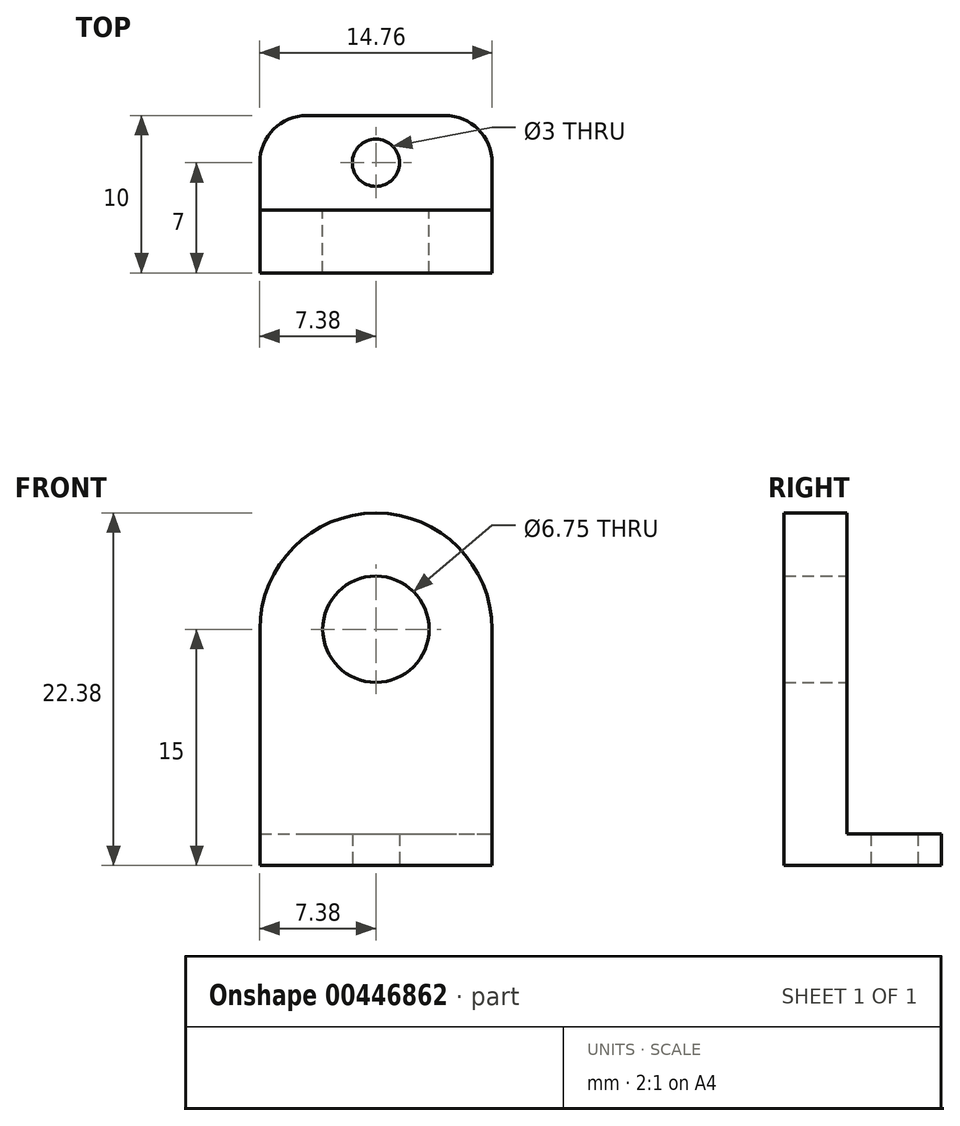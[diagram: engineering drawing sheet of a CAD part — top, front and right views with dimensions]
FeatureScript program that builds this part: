
annotation { "Feature Type Name" : "Feature", "Feature Type Description" : "" }
export const myFeature = defineFeature(function(context is Context, id is Id, definition is map)
    precondition{}
    {
        {
            var Q0;
            Q0=qCreatedBy(makeId("Front.planeOp"),FACE);
            var sketch = newSketch(context, id + "F0", { "sketchPlane" : qUnion([Q0])});
            skCircle(sketch, "E0", {"center": v(0, 0) * mm, "radius": 3.38 * mm});
            skCircle(sketch, "E1", {"center": v(0, 0) * mm, "radius": 7.38 * mm});
            skLineSegment(sketch, "E2", {"start": v(7.37, 0) * mm, "end": v(7.37, -15) * mm});
            skLineSegment(sketch, "E3", {"start": v(-7.38, 0) * mm, "end": v(-7.38, -15) * mm});
            skLineSegment(sketch, "E4", {"start": v(-7.37, -15) * mm, "end": v(7.37, -15) * mm});
            skSolve(sketch);
        }
        {
            var Q0;
            {var subQ0=sQuery(id+"F0.wireOp",EDGE,"E2");Q0=makeQuery(id+"F0.imprint","IMPRINT",FACE,{"disambiguationData":[TD([[makeQuery(id+"F0.imprint","IMPRINT",EDGE,{"derivedFrom":subQ0}),-1.0]])]});}
            var Q1;
            Q1=makeQuery(id+"F0.imprint","IMPRINT",FACE,{"disambiguationData":[TD([[makeQuery(id+"F0.imprint","IMPRINT",EDGE,{"derivedFrom":sQuery(id+"F0.wireOp",EDGE,"E0")}),-1.0]])]});
            extrude(context, id + "F1", {"entities" : qUnion([Q0, Q1]), "depth" : 4 * mm});
        }
        {
            var Q0;
            Q0=makeQuery(id+"F1.opExtrude","SWEPT_FACE",FACE,{"disambiguationData":[OSD([sQuery(id+"F0.wireOp",EDGE,"E4")])]});
            var sketch = newSketch(context, id + "F2", { "sketchPlane" : qUnion([Q0])});
            skLineSegment(sketch, "E5.bottom", {"start": v(-7.37, 4) * mm, "end": v(7.37, 4) * mm});
            skLineSegment(sketch, "E6.bottom", {"start": v(-7.37, 0) * mm, "end": v(7.37, 0) * mm});
            skLineSegment(sketch, "E6.top", {"start": v(-7.37, -6) * mm, "end": v(7.38, -6) * mm});
            skLineSegment(sketch, "E6.left", {"start": v(-7.37, 0) * mm, "end": v(-7.37, -6) * mm});
            skLineSegment(sketch, "E6.right", {"start": v(7.37, 0) * mm, "end": v(7.37, -6) * mm});
            skPoint(sketch, "E7", {"position": v(0, -3) * mm});
            skPoint(sketch, "E7.positionSnap0", {"position": v(-7.37, -3) * mm});
            skPoint(sketch, "E7.positionSnap1", {"position": v(0, -6) * mm});
            skSolve(sketch);
        }
        {
            var Q0;
            Q0=makeQuery(id+"F2.imprint","IMPRINT",FACE,{"disambiguationData":[TD([[makeQuery(id+"F2.imprint","IMPRINT",EDGE,{"derivedFrom":sQuery(id+"F2.wireOp",EDGE,"E6.bottom")}),-1.0]])]});
            var Q1;
            Q1=makeQuery(id+"F2.imprint","IMPRINT",FACE,{"disambiguationData":[TD([[makeQuery(id+"F2.imprint","IMPRINT",EDGE,{"derivedFrom":sQuery(id+"F2.wireOp",EDGE,"E5.bottom")}),-1.0]])]});
            var Q2;
            Q2=makeQuery(id+"F2.imprint","IMPRINT",FACE,{"disambiguationData":[TD([[makeQuery(id+"F2.imprint","IMPRINT",EDGE,{"derivedFrom":sQuery(id+"F2.wireOp",EDGE,"E5.bottom")}),1.0]])]});
            extrude(context, id + "F3", {"entities" : qUnion([Q0, Q1, Q2]), "operationType" : NewBodyOperationType.ADD, "oppositeDirection" : true, "depth" : 2 * mm});
        }
        {
            var Q0;
            Q0=makeQuery(id+"F3.opExtrude","SWEPT_EDGE",EDGE,{"disambiguationData":[OSD([sQuery(id+"F2.wireOp",EDGE,"E5.top"),sQuery(id+"F2.wireOp",EDGE,"E5.left")])]});
            var Q1;
            Q1=makeQuery(id+"F3.opExtrude","SWEPT_EDGE",EDGE,{"disambiguationData":[OSD([sQuery(id+"F2.wireOp",EDGE,"E5.top"),sQuery(id+"F2.wireOp",EDGE,"E5.right")])]});
            var Q2;
            Q2=makeQuery(id+"F3.opExtrude","SWEPT_EDGE",EDGE,{"disambiguationData":[OSD([sQuery(id+"F2.wireOp",EDGE,"E6.top"),sQuery(id+"F2.wireOp",EDGE,"E6.left")])]});
            var Q3;
            Q3=makeQuery(id+"F3.opExtrude","SWEPT_EDGE",EDGE,{"disambiguationData":[OSD([sQuery(id+"F2.wireOp",EDGE,"E6.top"),sQuery(id+"F2.wireOp",EDGE,"E6.right")])]});
            fillet(context, id + "F4", {"entities" : qUnion([Q0, Q1, Q2, Q3]), "radius" : 3 * mm, "tangentPropagation" : true, "allowEdgeOverflow" : false});
        }
        {
            var Q0;
            Q0=sQuery(id+"F2.wireOp",VERTEX,"E7");
            var Q1;
            Q1=makeQuery(id+"F1.opExtrude","SWEPT_BODY",BODY,{"disambiguationData":[OSD([sQuery(id+"F0.wireOp",EDGE,"E0"),sQuery(id+"F0.wireOp",EDGE,"E1"),sQuery(id+"F0.wireOp",EDGE,"E2"),sQuery(id+"F0.wireOp",EDGE,"E3"),sQuery(id+"F0.wireOp",EDGE,"E4")])]});
            hole(context, id + "F5", {"style" : HoleStyle.SIMPLE, "endStyle" : HoleEndStyle.THROUGH, "holeDiameter" : 3 * mm, "isTappedThrough" : true, "tappedDepth" : 12 * mm, "tapClearance" : 3, "locations" : qUnion([Q0]), "scope" : qUnion([Q1])});
        }
    });
